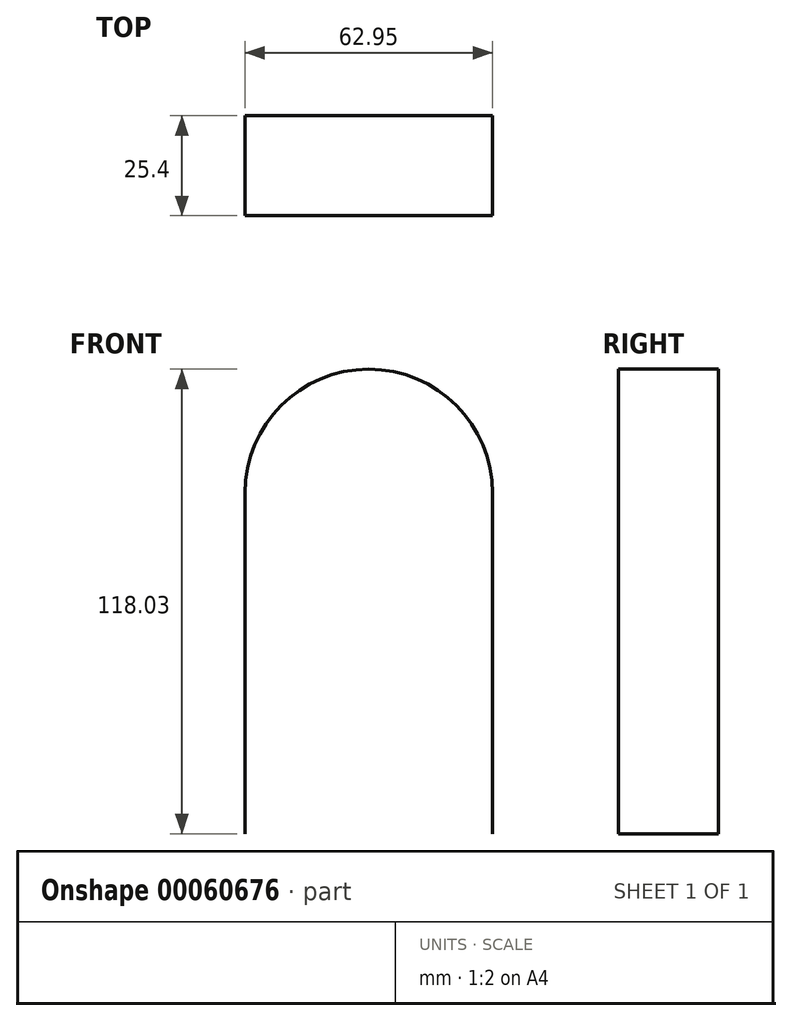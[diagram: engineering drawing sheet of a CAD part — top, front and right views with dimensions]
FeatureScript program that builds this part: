
annotation { "Feature Type Name" : "Feature", "Feature Type Description" : "" }
export const myFeature = defineFeature(function(context is Context, id is Id, definition is map)
    precondition{}
    {
        {
            var Q0;
            Q0=qCreatedBy(makeId("Front.planeOp"),FACE);
            var sketch = newSketch(context, id + "F0", { "sketchPlane" : qUnion([Q0])});
            skLineSegment(sketch, "E0", {"start": v(-40.06, 43.82) * mm, "end": v(-40.06, -42.74) * mm});
            skLineSegment(sketch, "E1", {"start": v(22.9, 43.82) * mm, "end": v(22.9, -42.74) * mm});
            skArc(sketch, "E2", {"start": v(22.9, 43.82) * mm, "mid": v(-8.58, 75.3) * mm, "end": v(-40.06, 43.82) * mm});
            skSolve(sketch);
        }
        {
            var Q0;
            Q0=sQuery(id+"F0.wireOp",EDGE,"E0");
            var Q1;
            Q1=sQuery(id+"F0.wireOp",EDGE,"E2");
            var Q2;
            Q2=sQuery(id+"F0.wireOp",EDGE,"E1");
            extrude(context, id + "F1", {"bodyType" : ToolBodyType.SURFACE, "surfaceEntities" : qUnion([Q0, Q1, Q2]), "depth" : 25.4 * mm});
        }
    });
